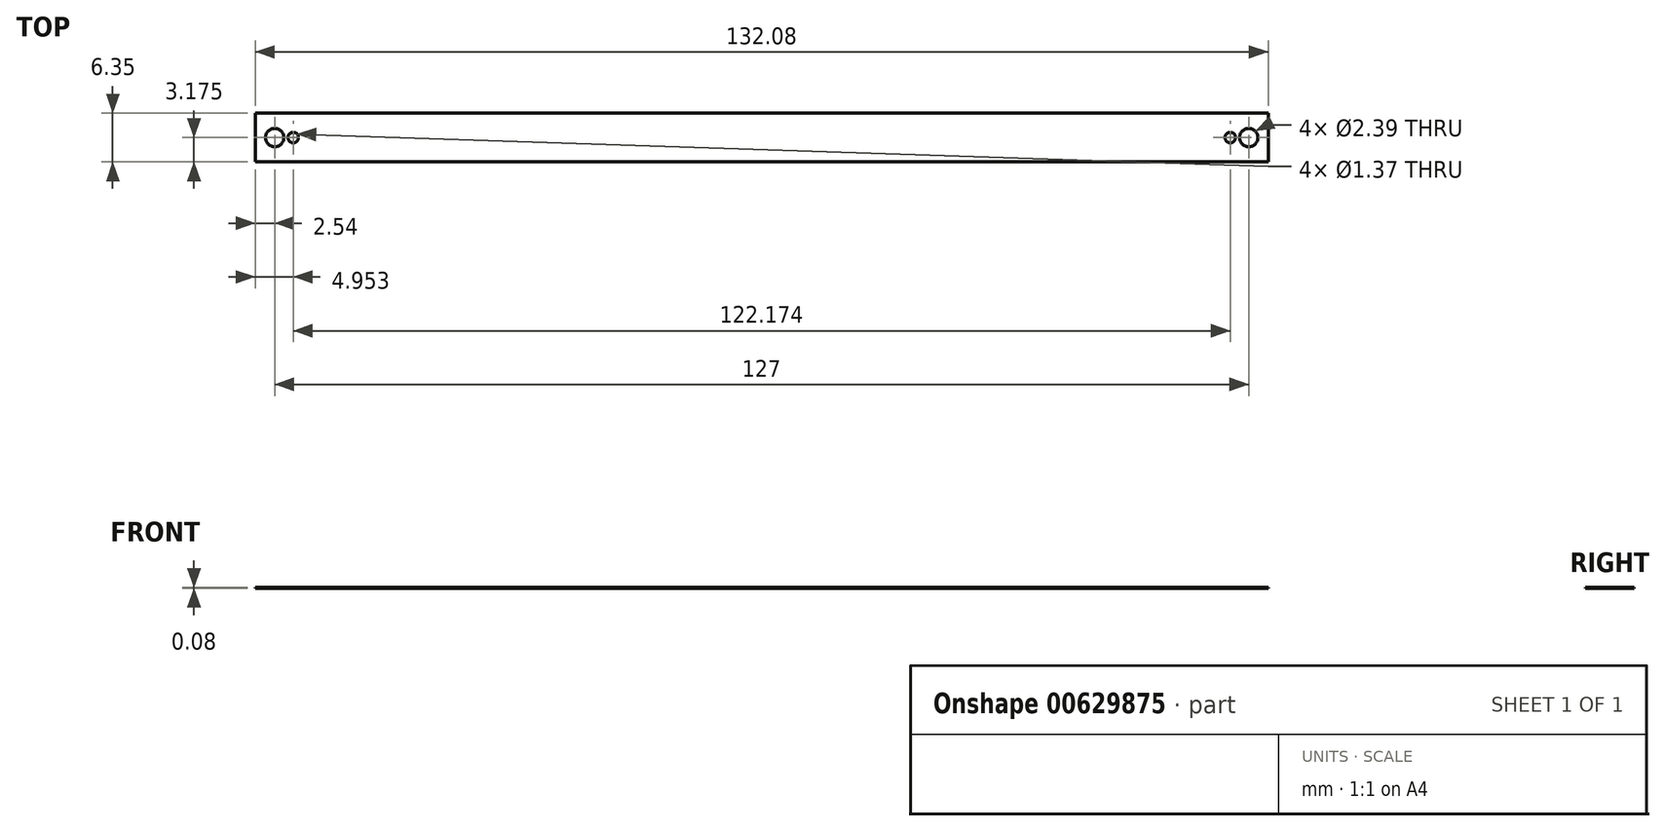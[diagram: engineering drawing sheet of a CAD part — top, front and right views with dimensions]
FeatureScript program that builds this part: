
annotation { "Feature Type Name" : "Feature", "Feature Type Description" : "" }
export const myFeature = defineFeature(function(context is Context, id is Id, definition is map)
    precondition{}
    {
        {
            var Q0;
            Q0=qCreatedBy(makeId("Top.planeOp"),FACE);
            var sketch = newSketch(context, id + "F0", { "sketchPlane" : qUnion([Q0])});
            skLineSegment(sketch, "E0.bottom", {"start": v(0, 0) * mm, "end": v(132.08, 0) * mm});
            skLineSegment(sketch, "E0.top", {"start": v(0, 6.35) * mm, "end": v(132.08, 6.35) * mm});
            skLineSegment(sketch, "E0.left", {"start": v(0, 0) * mm, "end": v(0, 6.35) * mm});
            skLineSegment(sketch, "E0.right", {"start": v(132.08, 0) * mm, "end": v(132.08, 6.35) * mm});
            skLineSegment(sketch, "E1", {"start": v(66.04, 6.35) * mm, "end": v(66.04, -11.63) * mm, "construction": true});
            skPoint(sketch, "E1.endSnap0", {"position": v(66.04, 0) * mm});
            skLineSegment(sketch, "E2", {"start": v(0, 3.18) * mm, "end": v(132.08, 3.18) * mm, "construction": true});
            skCircle(sketch, "E3", {"center": v(2.54, 3.18) * mm, "radius": 1.2 * mm});
            skCircle(sketch, "E4", {"center": v(4.95, 3.18) * mm, "radius": 0.69 * mm});
            skCircle(sketch, "E5.MirrorC", {"center": v(129.54, 3.17) * mm, "radius": 1.2 * mm});
            skCircle(sketch, "E6.MirrorC", {"center": v(127.13, 3.17) * mm, "radius": 0.69 * mm});
            skSolve(sketch);
        }
        {
            var Q0;
            Q0=makeQuery(id+"F0.imprint","IMPRINT",FACE,{"disambiguationData":[TD([[makeQuery(id+"F0.imprint","IMPRINT",EDGE,{"derivedFrom":sQuery(id+"F0.wireOp",EDGE,"E0.bottom")}),1.0]])]});
            extrude(context, id + "F1", {"entities" : qUnion([Q0]), "depth" : 0.08 * mm, "offsetDistance" : 25.4 * mm});
        }
        {
            var Q0;
            Q0=makeQuery(id+"F1.opExtrude","SWEPT_BODY",BODY,{"disambiguationData":[OSD([sQuery(id+"F0.wireOp",EDGE,"E0.bottom"),sQuery(id+"F0.wireOp",EDGE,"E0.top"),sQuery(id+"F0.wireOp",EDGE,"E0.left"),sQuery(id+"F0.wireOp",EDGE,"E0.right"),sQuery(id+"F0.wireOp",EDGE,"E3"),sQuery(id+"F0.wireOp",EDGE,"E4"),sQuery(id+"F0.wireOp",EDGE,"E6.MirrorC"),sQuery(id+"F0.wireOp",EDGE,"E5.MirrorC"),sQuery(id+"F0.wireOp",EDGE,"mCIEcZMN-lirI-KJGn-mpDW-QpH0F6nmvhsA"),sQuery(id+"F0.wireOp",EDGE,"31966a0d-8648-418d-8b7c-45f3307341bd0.MirrorC")])]});
            transform(context, id + "F2", {"entities" : qUnion([Q0]), "transformType" : TransformType.TRANSLATION_3D, "dx" : 0 * mm, "dy" : 0 * mm, "dz" : 0 * mm, "makeCopy" : true});
        }
    });
